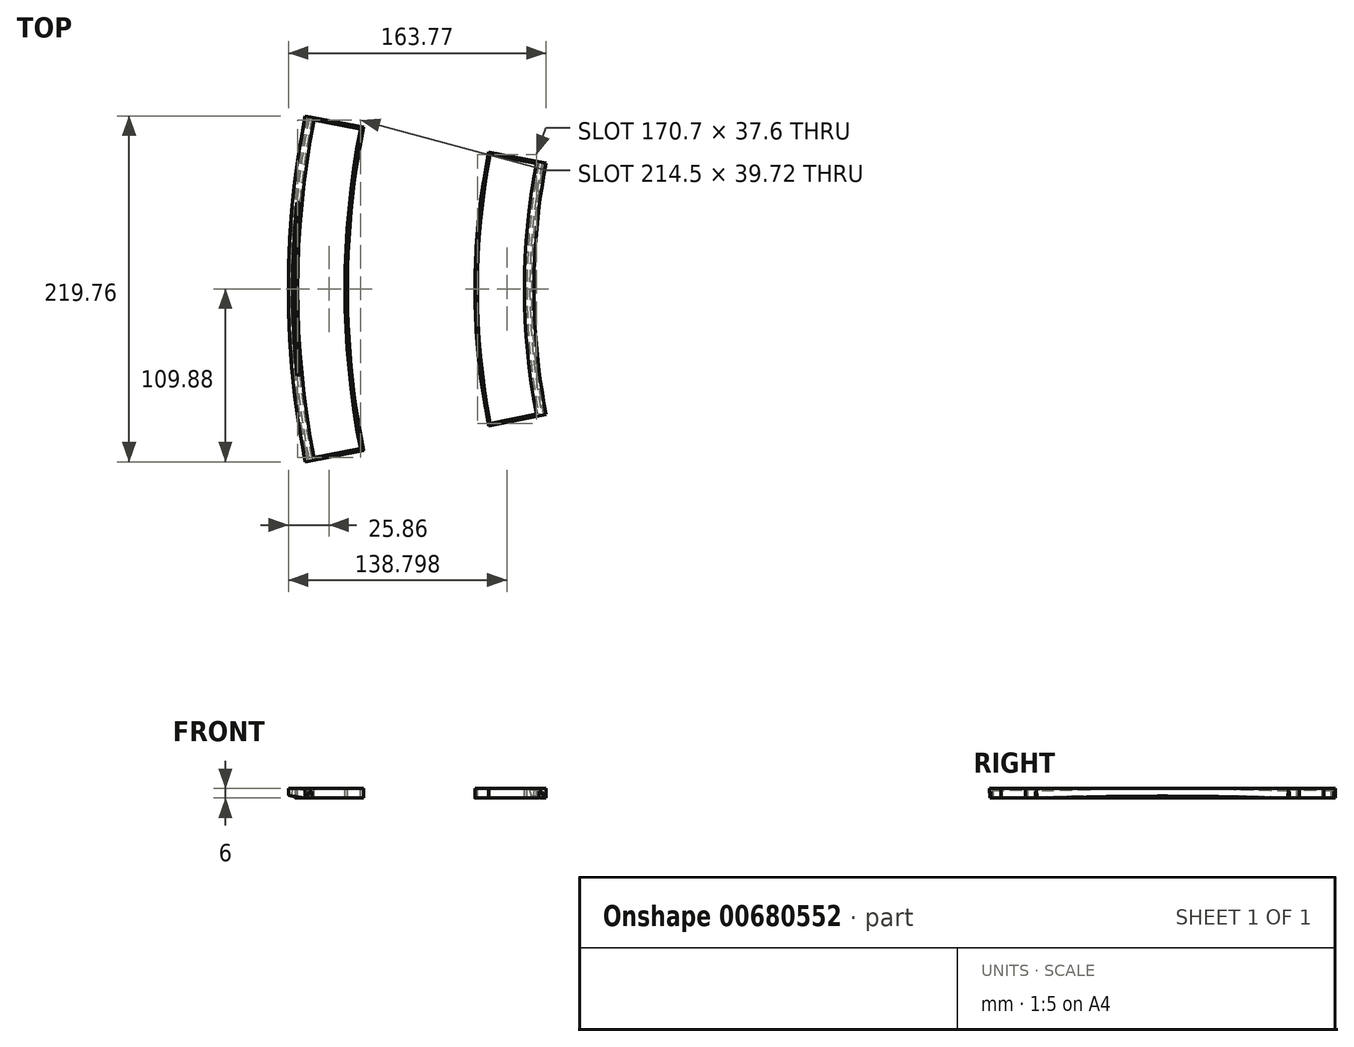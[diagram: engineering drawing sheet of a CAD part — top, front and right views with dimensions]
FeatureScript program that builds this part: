
annotation { "Feature Type Name" : "Feature", "Feature Type Description" : "" }
export const myFeature = defineFeature(function(context is Context, id is Id, definition is map)
    precondition{}
    {
        {
            var Q0;
            Q0=qCreatedBy(makeId("Front.planeOp"),FACE);
            var sketch = newSketch(context, id + "F0", { "sketchPlane" : qUnion([Q0])});
            skLineSegment(sketch, "E0", {"start": v(0, 1.91) * mm, "end": v(570.67, 0) * mm});
            skLineSegment(sketch, "E1", {"start": v(570.67, 0) * mm, "end": v(553.13, -97.53) * mm});
            skLineSegment(sketch, "E2", {"start": v(553.13, -97.53) * mm, "end": v(0, 1.91) * mm});
            skLineSegment(sketch, "E3", {"start": v(0, 1.91) * mm, "end": v(0.03, 10.91) * mm});
            skLineSegment(sketch, "E4", {"start": v(0.03, 10.91) * mm, "end": v(156.03, 10.39) * mm});
            skLineSegment(sketch, "E5", {"start": v(156.03, 10.39) * mm, "end": v(156, 1.39) * mm});
            skLineSegment(sketch, "E6", {"start": v(156, 1.39) * mm, "end": v(155.97, -7.61) * mm});
            skLineSegment(sketch, "E7", {"start": v(155.97, -7.61) * mm, "end": v(-0.03, -7.09) * mm});
            skLineSegment(sketch, "E8", {"start": v(-0.03, -7.09) * mm, "end": v(0, 1.91) * mm});
            skSolve(sketch);
        }
        {
            var Q0;
            {var subQ0=sQuery(id+"F0.wireOp",EDGE,"E3");Q0=makeQuery(id+"F0.imprint","IMPRINT",FACE,{"disambiguationData":[TD([[makeQuery(id+"F0.imprint","IMPRINT",EDGE,{"derivedFrom":subQ0}),-1.0]])]});}
            var Q1;
            {var subQ3=sQuery(id+"F0.wireOp",EDGE,"E6");Q1=makeQuery(id+"F0.imprint","IMPRINT",FACE,{"disambiguationData":[TD([[makeQuery(id+"F0.imprint","IMPRINT",EDGE,{"derivedFrom":subQ3}),-1.0]])]});}
            var Q2;
            {var subQ0=sQuery(id+"F0.wireOp",EDGE,"E8");Q2=makeQuery(id+"F0.imprint","IMPRINT",FACE,{"disambiguationData":[TD([[makeQuery(id+"F0.imprint","IMPRINT",EDGE,{"derivedFrom":subQ0}),-1.0]])]});}
            var Q3;
            Q3=sQuery(id+"F0.wireOp",EDGE,"E1");
            revolve(context, id + "F1", {"entities" : qUnion([Q0, Q1, Q2]), "axis" : qUnion([Q3]), "revolveType" : RevolveType.SYMMETRIC, "angle" : 22.5 * degree});
        }
        {
            var Q0;
            Q0=qCreatedBy(makeId("Front.planeOp"),FACE);
            var sketch = newSketch(context, id + "F2", { "sketchPlane" : qUnion([Q0])});
            skLineSegment(sketch, "E9.bottom", {"start": v(-6.73, 24.2) * mm, "end": v(170.86, 24.2) * mm});
            skLineSegment(sketch, "E9.top", {"start": v(-6.73, 7) * mm, "end": v(170.86, 7) * mm});
            skLineSegment(sketch, "E9.left", {"start": v(-6.73, 24.2) * mm, "end": v(-6.73, 7) * mm});
            skLineSegment(sketch, "E9.right", {"start": v(170.86, 24.2) * mm, "end": v(170.86, 7) * mm});
            skLineSegment(sketch, "E10.bottom", {"start": v(-6.11, 1) * mm, "end": v(170.86, 1) * mm});
            skLineSegment(sketch, "E10.top", {"start": v(-6.11, -14.01) * mm, "end": v(170.86, -14.01) * mm});
            skLineSegment(sketch, "E10.left", {"start": v(-6.11, 1) * mm, "end": v(-6.11, -14.01) * mm});
            skLineSegment(sketch, "E10.right", {"start": v(170.86, 1) * mm, "end": v(170.86, -14.01) * mm});
            skSolve(sketch);
        }
        {
            var Q0;
            Q0=makeQuery(id+"F2.imprint","IMPRINT",FACE,{"disambiguationData":[TD([[makeQuery(id+"F2.imprint","IMPRINT",EDGE,{"derivedFrom":sQuery(id+"F2.wireOp",EDGE,"E9.bottom")}),-1.0]])]});
            var Q1;
            Q1=makeQuery(id+"F2.imprint","IMPRINT",FACE,{"disambiguationData":[TD([[makeQuery(id+"F2.imprint","IMPRINT",EDGE,{"derivedFrom":sQuery(id+"F2.wireOp",EDGE,"E10.bottom")}),-1.0]])]});
            extrude(context, id + "F3", {"entities" : qUnion([Q0, Q1]), "operationType" : NewBodyOperationType.REMOVE, "endBound" : BoundingType.SYMMETRIC, "depth" : 256 * mm, "offsetDistance" : 25 * mm});
        }
        {
            var Q0;
            Q0=qCreatedBy(makeId("Front.planeOp"),FACE);
            var sketch = newSketch(context, id + "F4", { "sketchPlane" : qUnion([Q0])});
            skLineSegment(sketch, "E11", {"start": v(570.67, 0) * mm, "end": v(553.13, -97.53) * mm});
            skLineSegment(sketch, "E12", {"start": v(553.13, -97.53) * mm, "end": v(0, 1.91) * mm});
            skLineSegment(sketch, "E13", {"start": v(0, 2.71) * mm, "end": v(1.7, 2.71) * mm});
            skLineSegment(sketch, "E14", {"start": v(1.7, 2.71) * mm, "end": v(2.7, 7.22) * mm});
            skLineSegment(sketch, "E15", {"start": v(2.7, 7.22) * mm, "end": v(4.5, 7.21) * mm});
            skLineSegment(sketch, "E16", {"start": v(4.5, 7.21) * mm, "end": v(4.5, 2.71) * mm});
            skLineSegment(sketch, "E17", {"start": v(4.5, 2.71) * mm, "end": v(1.7, 2.71) * mm});
            skLineSegment(sketch, "E18", {"start": v(156, 1.39) * mm, "end": v(156, 2.19) * mm});
            skLineSegment(sketch, "E19", {"start": v(156, 2.19) * mm, "end": v(154.3, 2.19) * mm});
            skLineSegment(sketch, "E20", {"start": v(154.3, 2.19) * mm, "end": v(153.3, 6.69) * mm});
            skLineSegment(sketch, "E21", {"start": v(153.3, 6.69) * mm, "end": v(151.5, 6.7) * mm});
            skLineSegment(sketch, "E22", {"start": v(151.5, 6.7) * mm, "end": v(151.49, 2.19) * mm});
            skLineSegment(sketch, "E23", {"start": v(151.49, 2.19) * mm, "end": v(154.3, 2.19) * mm});
            skLineSegment(sketch, "E24", {"start": v(4.5, 2.71) * mm, "end": v(4.48, -0.62) * mm});
            skLineSegment(sketch, "E25", {"start": v(4.48, -0.62) * mm, "end": v(0, -0.62) * mm});
            skLineSegment(sketch, "E26", {"start": v(151.49, 2.19) * mm, "end": v(151.47, -1.83) * mm});
            skLineSegment(sketch, "E27", {"start": v(151.47, -1.83) * mm, "end": v(155.99, -1.83) * mm});
            skLineSegment(sketch, "E28", {"start": v(155.99, -1.83) * mm, "end": v(156, 1.39) * mm});
            skLineSegment(sketch, "E29", {"start": v(0, 2.71) * mm, "end": v(-1.68, 2.72) * mm});
            skLineSegment(sketch, "E30", {"start": v(-1.68, 2.72) * mm, "end": v(-1.68, 1.05) * mm});
            skLineSegment(sketch, "E31", {"start": v(-1.68, 1.05) * mm, "end": v(-1.68, -0.52) * mm});
            skLineSegment(sketch, "E32", {"start": v(-1.68, -0.52) * mm, "end": v(0, -0.62) * mm});
            skSolve(sketch);
        }
        {
            var Q0;
            Q0=makeQuery(id+"F4.imprint","IMPRINT",FACE,{"disambiguationData":[TD([[makeQuery(id+"F4.imprint","IMPRINT",EDGE,{"derivedFrom":sQuery(id+"F4.wireOp",EDGE,"E18")}),1.0]])]});
            var Q1;
            Q1=makeQuery(id+"F4.imprint","IMPRINT",FACE,{"disambiguationData":[TD([[makeQuery(id+"F4.imprint","IMPRINT",EDGE,{"derivedFrom":sQuery(id+"F4.wireOp",EDGE,"E20")}),1.0]])]});
            var Q2;
            Q2=makeQuery(id+"F4.imprint","IMPRINT",FACE,{"disambiguationData":[TD([[makeQuery(id+"F4.imprint","IMPRINT",EDGE,{"derivedFrom":sQuery(id+"F4.wireOp",EDGE,"E13")}),-1.0]])]});
            var Q3;
            Q3=makeQuery(id+"F4.imprint","IMPRINT",FACE,{"disambiguationData":[TD([[makeQuery(id+"F4.imprint","IMPRINT",EDGE,{"derivedFrom":sQuery(id+"F4.wireOp",EDGE,"E14")}),-1.0]])]});
            var Q4;
            Q4=sQuery(id+"F4.wireOp",EDGE,"E11");
            revolve(context, id + "F5", {"operationType" : NewBodyOperationType.REMOVE, "entities" : qUnion([Q0, Q1, Q2, Q3]), "axis" : qUnion([Q4]), "revolveType" : RevolveType.SYMMETRIC, "angle" : 30 * degree});
        }
        {
            var Q0;
            Q0=qCreatedBy(makeId("Front.planeOp"),FACE);
            var sketch = newSketch(context, id + "F6", { "sketchPlane" : qUnion([Q0])});
            skLineSegment(sketch, "E33", {"start": v(0, 1.91) * mm, "end": v(553.13, -97.53) * mm});
            skLineSegment(sketch, "E34", {"start": v(559.94, -59.66) * mm, "end": v(553.13, -97.53) * mm});
            skLineSegment(sketch, "E35", {"start": v(1.7, 2.71) * mm, "end": v(2.7, 7.2) * mm});
            skLineSegment(sketch, "E36", {"start": v(2.7, 7.2) * mm, "end": v(4.5, 7.2) * mm});
            skLineSegment(sketch, "E37", {"start": v(4.5, 7.2) * mm, "end": v(4.48, 2.7) * mm});
            skLineSegment(sketch, "E38", {"start": v(4.48, 2.7) * mm, "end": v(1.7, 2.71) * mm});
            skLineSegment(sketch, "E39", {"start": v(2.7, 7.2) * mm, "end": v(3.12, 9.1) * mm});
            skLineSegment(sketch, "E40", {"start": v(3.12, 9.1) * mm, "end": v(4.5, 9.1) * mm});
            skLineSegment(sketch, "E41", {"start": v(4.5, 9.1) * mm, "end": v(4.5, 7.2) * mm});
            skSolve(sketch);
        }
        {
            var Q0;
            Q0=makeQuery(id+"F6.imprint","IMPRINT",FACE,{"disambiguationData":[TD([[makeQuery(id+"F6.imprint","IMPRINT",EDGE,{"derivedFrom":sQuery(id+"F6.wireOp",EDGE,"E36")}),1.0]])]});
            var Q1;
            Q1=makeQuery(id+"F6.imprint","IMPRINT",FACE,{"disambiguationData":[TD([[makeQuery(id+"F6.imprint","IMPRINT",EDGE,{"derivedFrom":sQuery(id+"F6.wireOp",EDGE,"E35")}),-1.0]])]});
            var Q2;
            Q2=sQuery(id+"F6.wireOp",EDGE,"E34");
            revolve(context, id + "F7", {"operationType" : NewBodyOperationType.REMOVE, "entities" : qUnion([Q0, Q1]), "axis" : qUnion([Q2]), "revolveType" : RevolveType.SYMMETRIC, "angle" : 11.25 * degree});
        }
        {
            var Q0;
            Q0=makeQuery(id+"F3.boolean.opBoolean","COPY",FACE,{"derivedFrom":makeQuery(id+"F3.opExtrude","SWEPT_FACE",FACE,{"disambiguationData":[OSD([sQuery(id+"F2.wireOp",EDGE,"E9.top")])]})});
            var sketch = newSketch(context, id + "F8", { "sketchPlane" : qUnion([Q0])});
            skArc(sketch, "E42", {"start": v(16.28, 107.25) * mm, "mid": v(6, 0) * mm, "end": v(16.28, -107.25) * mm});
            skArc(sketch, "E43", {"start": v(45.72, 101.49) * mm, "mid": v(36, 0) * mm, "end": v(45.72, -101.49) * mm});
            skArc(sketch, "E44", {"start": v(51.6, 100.34) * mm, "mid": v(44.44, 50.77) * mm, "end": v(42, 0.75) * mm});
            skArc(sketch, "E45", {"start": v(122.27, 86.5) * mm, "mid": v(116.1, 43.82) * mm, "end": v(114, 0.75) * mm});
            skArc(sketch, "E46", {"start": v(128.16, 85.35) * mm, "mid": v(120, 0) * mm, "end": v(128.16, -85.35) * mm});
            skArc(sketch, "E47", {"start": v(157.6, 79.59) * mm, "mid": v(150, 0) * mm, "end": v(157.6, -79.59) * mm});
            skLineSegment(sketch, "E48", {"start": v(16.28, 107.25) * mm, "end": v(45.72, 101.49) * mm});
            skLineSegment(sketch, "E49", {"start": v(51.6, 100.34) * mm, "end": v(122.27, 86.5) * mm});
            skLineSegment(sketch, "E50", {"start": v(128.16, 85.35) * mm, "end": v(157.6, 79.59) * mm});
            skLineSegment(sketch, "E51", {"start": v(16.28, -107.25) * mm, "end": v(45.72, -101.49) * mm});
            skLineSegment(sketch, "E52", {"start": v(51.6, -100.34) * mm, "end": v(122.27, -86.5) * mm});
            skLineSegment(sketch, "E53", {"start": v(128.16, -85.35) * mm, "end": v(157.6, -79.59) * mm});
            skLineSegment(sketch, "E54", {"start": v(42, 0.75) * mm, "end": v(114, 0.75) * mm});
            skLineSegment(sketch, "E55", {"start": v(42, -0.75) * mm, "end": v(114, -0.75) * mm});
            skArc(sketch, "E56.trimOffspring", {"start": v(114, -0.75) * mm, "mid": v(116.1, -43.82) * mm, "end": v(122.27, -86.5) * mm});
            skArc(sketch, "E57.trimOffspring", {"start": v(42, -0.75) * mm, "mid": v(44.44, -50.77) * mm, "end": v(51.6, -100.34) * mm});
            skSolve(sketch);
        }
        {
            var Q0;
            Q0=makeQuery(id+"F8.imprint","IMPRINT",FACE,{"disambiguationData":[TD([[makeQuery(id+"F8.imprint","IMPRINT",EDGE,{"derivedFrom":sQuery(id+"F8.wireOp",EDGE,"E42")}),1.0]])]});
            var Q1;
            Q1=makeQuery(id+"F8.imprint","IMPRINT",FACE,{"disambiguationData":[TD([[makeQuery(id+"F8.imprint","IMPRINT",EDGE,{"derivedFrom":sQuery(id+"F8.wireOp",EDGE,"E44")}),1.0]])]});
            var Q2;
            Q2=makeQuery(id+"F8.imprint","IMPRINT",FACE,{"disambiguationData":[TD([[makeQuery(id+"F8.imprint","IMPRINT",EDGE,{"derivedFrom":sQuery(id+"F8.wireOp",EDGE,"E46")}),1.0]])]});
            var Q3;
            Q3=makeQuery(id+"F8.imprint","IMPRINT",FACE,{"disambiguationData":[TD([[makeQuery(id+"F8.imprint","IMPRINT",EDGE,{"derivedFrom":sQuery(id+"F8.wireOp",EDGE,"E52")}),1.0]])]});
            extrude(context, id + "F9", {"entities" : qUnion([Q0, Q1, Q2, Q3]), "operationType" : NewBodyOperationType.REMOVE, "endBound" : BoundingType.THROUGH_ALL, "oppositeDirection" : true, "depth" : 25 * mm, "offsetDistance" : 25 * mm});
        }
        {
            var Q0;
            Q0=qCreatedBy(makeId("Front.planeOp"),FACE);
            var sketch = newSketch(context, id + "F10", { "sketchPlane" : qUnion([Q0])});
            skLineSegment(sketch, "E58", {"start": v(0, 1.91) * mm, "end": v(499.78, -162.1) * mm});
            skLineSegment(sketch, "E59", {"start": v(499.78, -162.1) * mm, "end": v(528.06, -75.91) * mm});
            skLineSegment(sketch, "E60.bottom", {"start": v(37.5, 13.47) * mm, "end": v(40.5, 13.47) * mm});
            skLineSegment(sketch, "E60.top", {"start": v(37.5, -3.91) * mm, "end": v(40.5, -3.91) * mm});
            skLineSegment(sketch, "E60.left", {"start": v(37.5, 13.47) * mm, "end": v(37.5, -3.91) * mm});
            skLineSegment(sketch, "E60.right", {"start": v(40.5, 13.47) * mm, "end": v(40.5, -3.91) * mm});
            skLineSegment(sketch, "E61.bottom", {"start": v(115.5, 14.34) * mm, "end": v(118.5, 14.34) * mm});
            skLineSegment(sketch, "E61.top", {"start": v(115.5, -3.91) * mm, "end": v(118.5, -3.91) * mm});
            skLineSegment(sketch, "E61.left", {"start": v(115.5, 14.34) * mm, "end": v(115.5, -3.91) * mm});
            skLineSegment(sketch, "E61.right", {"start": v(118.5, 14.34) * mm, "end": v(118.5, -3.91) * mm});
            skLineSegment(sketch, "E62", {"start": v(40.5, 13.47) * mm, "end": v(115.5, 14.34) * mm});
            skLineSegment(sketch, "E63", {"start": v(40.5, -3.91) * mm, "end": v(115.5, -3.91) * mm});
            skSolve(sketch);
        }
        {
            var Q0;
            Q0=makeQuery(id+"F10.imprint","IMPRINT",FACE,{"disambiguationData":[TD([[makeQuery(id+"F10.imprint","IMPRINT",EDGE,{"derivedFrom":sQuery(id+"F10.wireOp",EDGE,"E60.bottom")}),-1.0]])]});
            var Q1;
            Q1=makeQuery(id+"F10.imprint","IMPRINT",FACE,{"disambiguationData":[TD([[makeQuery(id+"F10.imprint","IMPRINT",EDGE,{"derivedFrom":sQuery(id+"F10.wireOp",EDGE,"E61.bottom")}),-1.0]])]});
            var Q2;
            Q2=makeQuery(id+"F10.imprint","IMPRINT",FACE,{"disambiguationData":[TD([[makeQuery(id+"F10.imprint","IMPRINT",EDGE,{"derivedFrom":sQuery(id+"F10.wireOp",EDGE,"E60.right")}),1.0]])]});
            var Q3;
            Q3=sQuery(id+"F10.wireOp",EDGE,"E59");
            revolve(context, id + "F11", {"operationType" : NewBodyOperationType.REMOVE, "entities" : qUnion([Q0, Q1, Q2]), "axis" : qUnion([Q3]), "revolveType" : RevolveType.SYMMETRIC, "angle" : 30 * degree});
        }
    });
